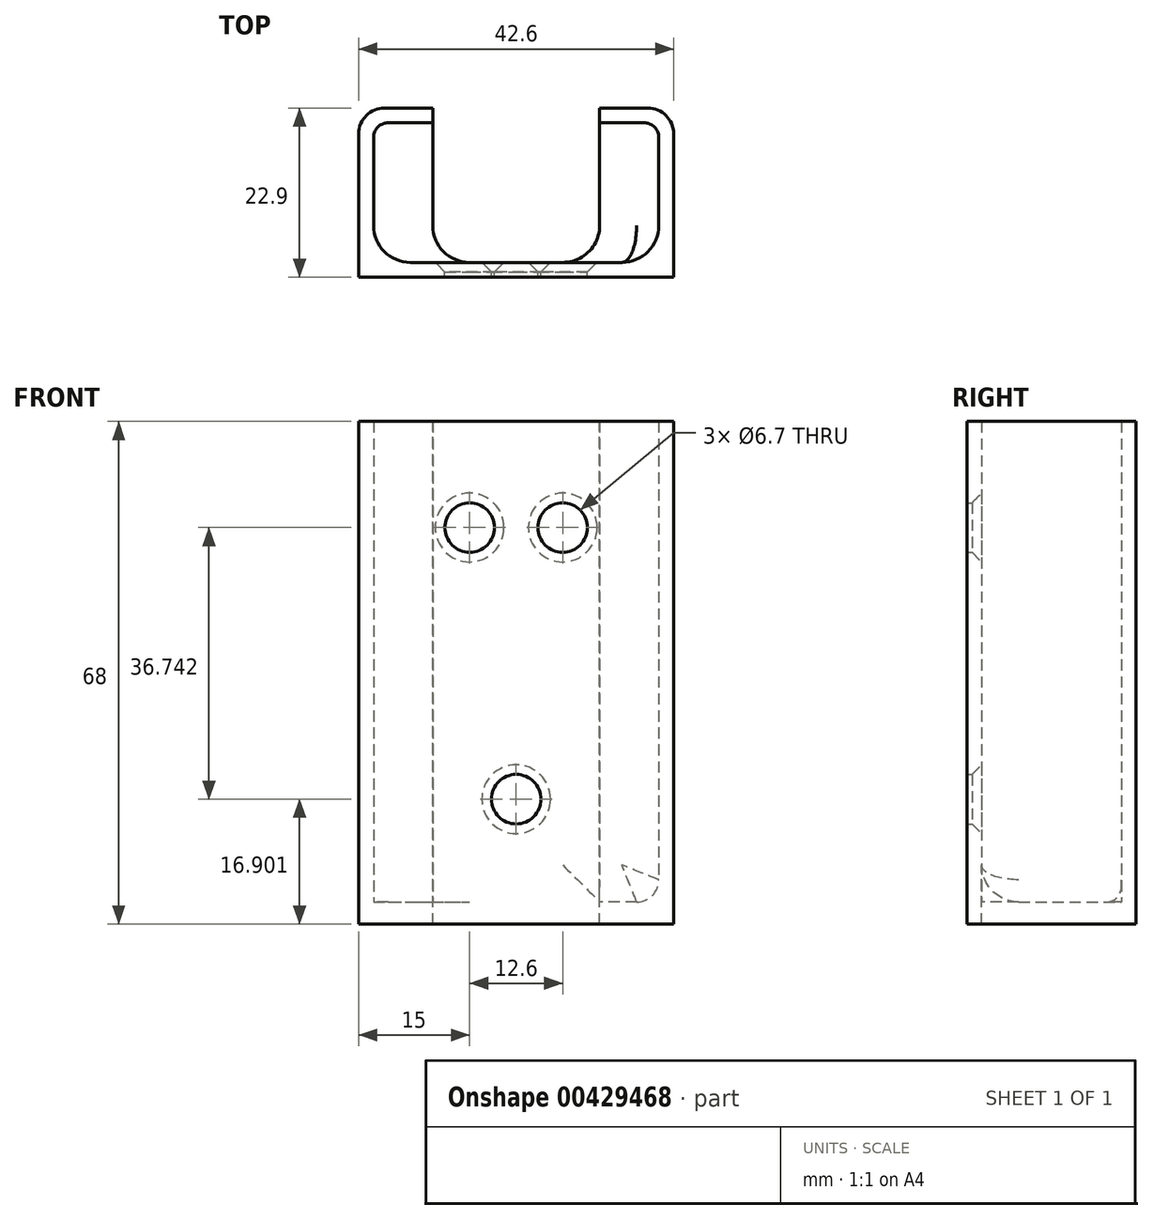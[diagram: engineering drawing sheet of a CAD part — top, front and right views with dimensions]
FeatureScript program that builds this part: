
annotation { "Feature Type Name" : "Feature", "Feature Type Description" : "" }
export const myFeature = defineFeature(function(context is Context, id is Id, definition is map)
    precondition{}
    {
        {
            var Q0;
            Q0=qCreatedBy(makeId("Top.planeOp"),FACE);
            var sketch = newSketch(context, id + "F0", { "sketchPlane" : qUnion([Q0])});
            skLineSegment(sketch, "E0.bottom", {"start": v(19.3, -9.45) * mm, "end": v(-19.3, -9.45) * mm, "construction": true});
            skLineSegment(sketch, "E0.top", {"start": v(19.3, 9.45) * mm, "end": v(-19.3, 9.45) * mm, "construction": true});
            skLineSegment(sketch, "E0.left", {"start": v(19.3, -9.45) * mm, "end": v(19.3, 9.45) * mm, "construction": true});
            skLineSegment(sketch, "E0.right", {"start": v(-19.3, -9.45) * mm, "end": v(-19.3, 9.45) * mm, "construction": true});
            skPoint(sketch, "E0.middle", {"position": v(0, 0) * mm});
            skLineSegment(sketch, "E1.0", {"start": v(-21.3, -11.45) * mm, "end": v(-21.3, 11.45) * mm, "construction": true});
            skLineSegment(sketch, "E1.1", {"start": v(21.3, -11.45) * mm, "end": v(-21.3, -11.45) * mm, "construction": true});
            skLineSegment(sketch, "E1.2", {"start": v(21.3, -11.45) * mm, "end": v(21.3, 11.45) * mm, "construction": true});
            skLineSegment(sketch, "E1.3", {"start": v(21.3, 11.45) * mm, "end": v(-21.3, 11.45) * mm, "construction": true});
            skLineSegment(sketch, "E2", {"start": v(-19.3, 9.45) * mm, "end": v(-11.3, 9.45) * mm});
            skLineSegment(sketch, "E3", {"start": v(-11.3, 9.45) * mm, "end": v(-11.3, 11.45) * mm});
            skLineSegment(sketch, "E4", {"start": v(-11.3, 11.45) * mm, "end": v(-21.3, 11.45) * mm});
            skLineSegment(sketch, "E5", {"start": v(-21.3, -11.45) * mm, "end": v(21.3, -11.45) * mm});
            skLineSegment(sketch, "E6", {"start": v(21.3, 11.45) * mm, "end": v(21.3, -11.45) * mm});
            skLineSegment(sketch, "E7", {"start": v(-19.3, 9.45) * mm, "end": v(-19.3, -9.45) * mm});
            skLineSegment(sketch, "E8", {"start": v(19.3, -9.45) * mm, "end": v(19.3, 9.45) * mm});
            skLineSegment(sketch, "E9", {"start": v(19.3, 9.45) * mm, "end": v(11.3, 9.45) * mm});
            skLineSegment(sketch, "E10", {"start": v(11.3, 9.45) * mm, "end": v(11.3, 11.45) * mm});
            skLineSegment(sketch, "E11", {"start": v(11.3, 11.45) * mm, "end": v(21.3, 11.45) * mm});
            skLineSegment(sketch, "E12", {"start": v(-19.3, -9.45) * mm, "end": v(19.3, -9.45) * mm});
            skLineSegment(sketch, "E13", {"start": v(-21.3, 11.45) * mm, "end": v(-21.3, -11.45) * mm});
            skLineSegment(sketch, "E14", {"start": v(-11.3, 9.45) * mm, "end": v(-11.3, -9.45) * mm});
            skLineSegment(sketch, "E15", {"start": v(11.3, 9.45) * mm, "end": v(11.3, -9.45) * mm});
            skSolve(sketch);
        }
        {
            var Q0;
            Q0=makeQuery(id+"F0.imprint","IMPRINT",FACE,{"disambiguationData":[TD([[makeQuery(id+"F0.imprint","IMPRINT",EDGE,{"derivedFrom":sQuery(id+"F0.wireOp",EDGE,"E2")}),1.0]])]});
            var Q1;
            Q1=makeQuery(id+"F0.imprint","IMPRINT",FACE,{"disambiguationData":[TD([[makeQuery(id+"F0.imprint","IMPRINT",EDGE,{"derivedFrom":sQuery(id+"F0.wireOp",EDGE,"E2")}),-1.0]])]});
            var Q2;
            {var subQ0=sQuery(id+"F0.wireOp",EDGE,"E8");Q2=makeQuery(id+"F0.imprint","IMPRINT",FACE,{"disambiguationData":[TD([[makeQuery(id+"F0.imprint","IMPRINT",EDGE,{"derivedFrom":subQ0}),1.0]])]});}
            extrude(context, id + "F1", {"entities" : qUnion([Q0, Q1, Q2]), "oppositeDirection" : true, "depth" : 3 * mm});
        }
        {
            var Q0;
            Q0=makeQuery(id+"F0.imprint","IMPRINT",FACE,{"disambiguationData":[TD([[makeQuery(id+"F0.imprint","IMPRINT",EDGE,{"derivedFrom":sQuery(id+"F0.wireOp",EDGE,"E2")}),1.0]])]});
            extrude(context, id + "F2", {"entities" : qUnion([Q0]), "operationType" : NewBodyOperationType.ADD, "depth" : 65 * mm});
        }
        {
            var Q0;
            {var subQ0=sQuery(id+"F0.wireOp",EDGE,"E12");Q0=makeQuery(id+"F2.boolean.opBoolean","MERGE",FACE,{"derivedFrom":[makeQuery(id+"F1.opExtrude","SWEPT_FACE",FACE,{"disambiguationData":[OSD([subQ0])]}),makeQuery(id+"F2.opExtrude","SWEPT_FACE",FACE,{"disambiguationData":[OSD([subQ0])]})]});}
            var sketch = newSketch(context, id + "F3", { "sketchPlane" : qUnion([Q0])});
            skPoint(sketch, "E16", {"position": v(0, 13.9) * mm});
            skPoint(sketch, "E17", {"position": v(-6.3, 50.64) * mm});
            skPoint(sketch, "E18", {"position": v(6.3, 50.64) * mm});
            skSolve(sketch);
        }
        {
            var Q0;
            Q0=sQuery(id+"F3.wireOp",VERTEX,"E17");
            var Q1;
            Q1=sQuery(id+"F3.wireOp",VERTEX,"E18");
            var Q2;
            Q2=sQuery(id+"F3.wireOp",VERTEX,"E16");
            var Q3;
            Q3=makeQuery(id+"F1.opExtrude","SWEPT_BODY",BODY,{"disambiguationData":[OSD([sQuery(id+"F0.wireOp",EDGE,"E3"),sQuery(id+"F0.wireOp",EDGE,"E4"),sQuery(id+"F0.wireOp",EDGE,"E5"),sQuery(id+"F0.wireOp",EDGE,"E6"),sQuery(id+"F0.wireOp",EDGE,"E10"),sQuery(id+"F0.wireOp",EDGE,"E11"),sQuery(id+"F0.wireOp",EDGE,"E12"),sQuery(id+"F0.wireOp",EDGE,"E13"),sQuery(id+"F0.wireOp",EDGE,"E14"),sQuery(id+"F0.wireOp",EDGE,"E15")])]});
            hole(context, id + "F4", {"style" : HoleStyle.C_SINK, "endStyle" : HoleEndStyle.THROUGH, "holeDiameter" : 6.7 * mm, "cSinkDiameter" : 9.3 * mm, "cSinkAngle" : 90 * degree, "isTappedThrough" : true, "tappedDepth" : 12 * mm, "tapClearance" : 3, "startFromSketch" : true, "locations" : qUnion([Q0, Q1, Q2]), "scope" : qUnion([Q3])});
        }
        {
            var Q0;
            Q0=makeQuery(id+"F2.opExtrude","CAP_EDGE",EDGE,{"disambiguationData":[OSD([sQuery(id+"F0.wireOp",EDGE,"E7")])],"isStart":true});
            var Q1;
            Q1=makeQuery(id+"F2.opExtrude","CAP_EDGE",EDGE,{"disambiguationData":[OSD([sQuery(id+"F0.wireOp",EDGE,"E8")])],"isStart":true});
            fillet(context, id + "F5", {"entities" : qUnion([Q0, Q1]), "radius" : 3 * mm, "tangentPropagation" : true, "allowEdgeOverflow" : false});
        }
        {
            var Q0;
            Q0=makeQuery(id+"F2.opExtrude","SWEPT_EDGE",EDGE,{"disambiguationData":[OSD([sQuery(id+"F0.wireOp",EDGE,"E7"),sQuery(id+"F0.wireOp",EDGE,"E12")])]});
            var Q1;
            Q1=makeQuery(id+"F2.opExtrude","SWEPT_EDGE",EDGE,{"disambiguationData":[OSD([sQuery(id+"F0.wireOp",EDGE,"E8"),sQuery(id+"F0.wireOp",EDGE,"E12")])]});
            fillet(context, id + "F6", {"entities" : qUnion([Q0, Q1]), "radius" : 5 * mm, "tangentPropagation" : true, "allowEdgeOverflow" : false});
        }
        {
            var Q0;
            Q0=makeQuery(id+"F2.opExtrude","SWEPT_EDGE",EDGE,{"disambiguationData":[OSD([sQuery(id+"F0.wireOp",EDGE,"E8"),sQuery(id+"F0.wireOp",EDGE,"E9")])]});
            var Q1;
            Q1=makeQuery(id+"F2.opExtrude","SWEPT_EDGE",EDGE,{"disambiguationData":[OSD([sQuery(id+"F0.wireOp",EDGE,"E2"),sQuery(id+"F0.wireOp",EDGE,"E7")])]});
            fillet(context, id + "F7", {"entities" : qUnion([Q0, Q1]), "radius" : 2 * mm, "tangentPropagation" : true, "allowEdgeOverflow" : false});
        }
        {
            var Q0;
            {var subQ0=sQuery(id+"F0.wireOp",EDGE,"E11");var subQ1=sQuery(id+"F0.wireOp",EDGE,"E6");Q0=makeQuery(id+"F2.boolean.opBoolean","MERGE",EDGE,{"derivedFrom":[makeQuery(id+"F1.opExtrude","SWEPT_EDGE",EDGE,{"disambiguationData":[OSD([subQ1,subQ0])]}),makeQuery(id+"F2.opExtrude","SWEPT_EDGE",EDGE,{"disambiguationData":[OSD([subQ1,subQ0])]})]});}
            var Q1;
            {var subQ0=sQuery(id+"F0.wireOp",EDGE,"E13");var subQ1=sQuery(id+"F0.wireOp",EDGE,"E4");Q1=makeQuery(id+"F2.boolean.opBoolean","MERGE",EDGE,{"derivedFrom":[makeQuery(id+"F1.opExtrude","SWEPT_EDGE",EDGE,{"disambiguationData":[OSD([subQ1,subQ0])]}),makeQuery(id+"F2.opExtrude","SWEPT_EDGE",EDGE,{"disambiguationData":[OSD([subQ1,subQ0])]})]});}
            fillet(context, id + "F8", {"entities" : qUnion([Q0, Q1]), "radius" : 3.5 * mm, "tangentPropagation" : true, "allowEdgeOverflow" : false});
        }
        {
            var Q0;
            Q0=makeQuery(id+"F1.opExtrude","SWEPT_EDGE",EDGE,{"disambiguationData":[OSD([sQuery(id+"F0.wireOp",EDGE,"E12"),sQuery(id+"F0.wireOp",EDGE,"E15")])]});
            var Q1;
            Q1=makeQuery(id+"F1.opExtrude","SWEPT_EDGE",EDGE,{"disambiguationData":[OSD([sQuery(id+"F0.wireOp",EDGE,"E12"),sQuery(id+"F0.wireOp",EDGE,"E14")])]});
            fillet(context, id + "F9", {"entities" : qUnion([Q0, Q1]), "radius" : 5 * mm, "tangentPropagation" : true, "allowEdgeOverflow" : false});
        }
    });
